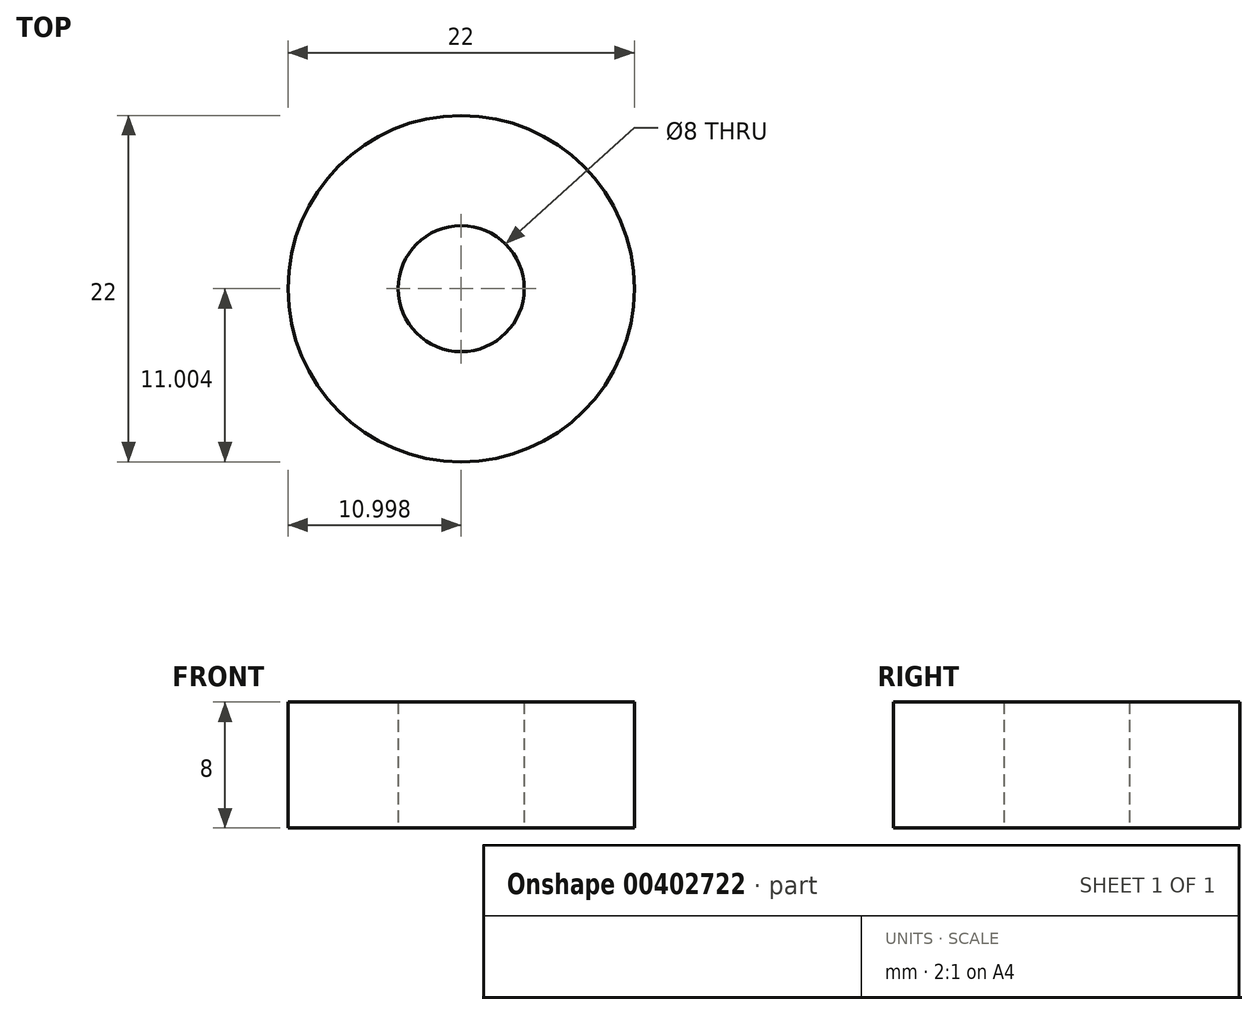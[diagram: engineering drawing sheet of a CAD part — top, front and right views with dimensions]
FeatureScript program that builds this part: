
annotation { "Feature Type Name" : "Feature", "Feature Type Description" : "" }
export const myFeature = defineFeature(function(context is Context, id is Id, definition is map)
    precondition{}
    {
        {
            var Q0;
            Q0=qCreatedBy(makeId("Top.planeOp"),FACE);
            var sketch = newSketch(context, id + "F0", { "sketchPlane" : qUnion([Q0])});
            skCircle(sketch, "E0", {"center": v(-60.72, 56.26) * mm, "radius": 11 * mm});
            skCircle(sketch, "E1", {"center": v(-60.72, 56.26) * mm, "radius": 4 * mm});
            skSolve(sketch);
        }
        {
            var Q0;
            Q0 = qSketchRegion(id + "F0", true);
            extrude(context, id + "F1", {"entities" : qUnion([Q0]), "depth" : 8 * mm});
        }
    });
